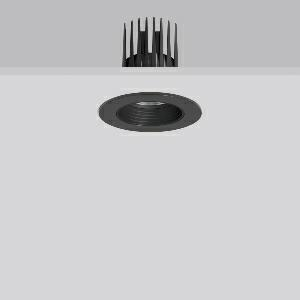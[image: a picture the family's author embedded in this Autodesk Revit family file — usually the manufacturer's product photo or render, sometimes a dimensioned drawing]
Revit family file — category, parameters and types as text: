
# Revit family: heledon_mini_e_901755_003_3_76_e8c0
name_source: partatom
category: Lighting Fixtures
units: mm (PartAtom-declared; Revit-internal decimal feet)

## family parameters
Cut with Voids When Loaded = No
Host = Face
Light Source = No
Part Type = Normal
Room Calculation Point = No
Round Connector Dimension = Use Diameter
Shared = No

## types (1)
- HELEDON mini E (1 x LED Modul 935, 2800 lm, 3500)
    Apparent Load = 29 VA
    Approval mark = CE
    CIE Flux Codes = 95 100 100 100 100
    Color Rendering = 92
    Color Temperature = 3500
    Default Elevation = 1800 mm
    Description = Series: HELEDON mini
Round recessed downlight. Housing: die-cast aluminium, powder-coated. Black plastic ring and recessed LED to prevent glare from the side. Optical assembly with lens made of plastic (polycarbonate) for the best homogeneous light distribution - can be changed without tools. Best colour rendering index Ra>90. Suitable for Recessed ceiling mounting. Installation without tools thanks to spring fastening system. Including separate LED converter with connecting cable 600 mm.High quality converter without flickering and stroboscopic effect. Through-wiring box (5 pole) available as accessory. The following accessories can be mounted without use of tools: interchangeable lenses, decorative glasses, honeycomb louvre, clear and frosted diffusers, white interchangeable plastic ring. 
Colour: deep black, matt (RAL 9005)
Diameter: 124 mm
Height: 3 mm
Cut-out diameter: 114 mm
Recess height: 170 mm
Luminaire: recess height: 120 mm
Lamp: LED
Socket: without socket
Colour temperature: 3500K
Colour rendering index (CRI): 92
System power: 29 W
Rated luminous flux: 2800 lm
Luminous efficiency: 97 lm/W
Control gear: Converter, dimmable, DALI
Protection class: II
Type of protection: IP 20
    Height = 0 mm  [stored 0 ft]
    Lamp = 1 x LED Modul 935
    Lamp Light Flux = 2800 lm
    Lamp count = 1
    Length = 124 mm  [stored 0.406824 ft]
    Lifetime = 50000 h
    Luminous efficacy = 97 lm/W
    Manufacturer = RZB
    ModVariant = No
    Model = 901755.003.3.76
    Mounting Place = Ceiling
    Mounting Type = Recessed
    Number of Poles = 1
    OnlyDefault = Yes
    Power Factor = 1
    Product Name = HELEDON mini E
    Product group = Recessed downlights
    ProductGroupID = 402
    Protection Class = Protection class II
    Protection Degree = IP 20
    RLX_Detail_Level = 1
    RLX_Emergency_Light_Flux = 0 lm
    RLX_Emergency_Type = 0
    RLX_Emergency_Type_DB = No
    RlxData = <blob elided: 133613 chars, md5=dd073a71>
    Socket = socket
    Standby Power = 0 W
    System Light Flux = 2800 lm
    System Power = 29 W
    Type Comments = Product without accessories
    Type Image = 901656.003.jpg
    URL = http://relux.com
    VarID = ---
    Voltage = 230 V
    Voltage Range = 220-240 V
    Weight = 0.00 kg
    Width = 0 mm  [stored 0 ft]

note: [stored X ft] marks values corroborated as IEEE doubles in the binary element streams (Revit-internal decimal feet)

## geometry (parser evidence)
native form markers: Blend x4, Sweep x12
no freeform markers — native parametric forms only
